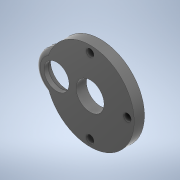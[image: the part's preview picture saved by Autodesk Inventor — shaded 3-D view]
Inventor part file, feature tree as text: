
AUTODESK INVENTOR PART (.ipt)
format: ipt  version: 2020 (Build 240168000, 168)  size: 160,256 bytes
history: native  units: in
note: dims shown in document units (in); Inventor stores cm internally (conversion verified against a paired STEP export)
features: extrude x2, sketch x2, fillet x1
ambient origin geometry x8: Origin, YZ Plane, XZ Plane, XY Plane, X Axis, Y Axis, Z Axis, Center Point
bodies: Solid1 (feature_tree)
feature tree (5):
  extrude  "Extrusion1"  Depth=0.75in
  extrude  "Extrusion2"  Depth=0.125in
  fillet  "Fillet1"  Radius=0.275in
  sketch  "Sketch1"  dims[d0=0.875in d1=0.75in]
  sketch  "Sketch2"  dims[d2=0.9in d3=0.125in d6=0.275in d7=0.0in d8=2.0in d11=0.2031in d14=0.1in d15=0.119in d16=0.0in d17=2.362in d18=0.125in d19=0.5in d20=0.0344in d21=0.5in d22=0.0344in]
